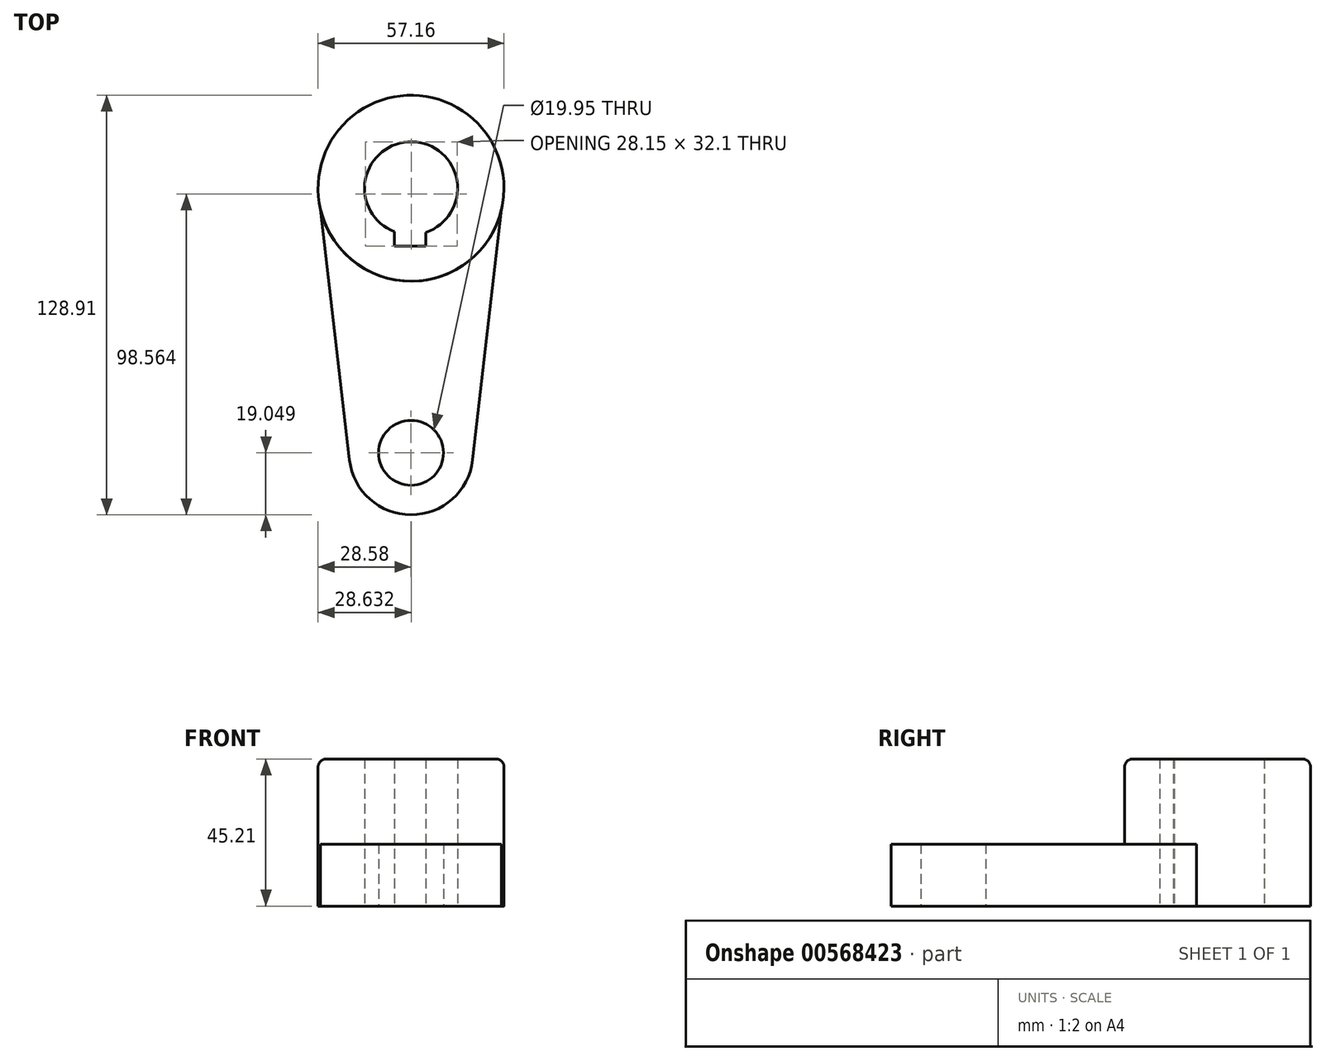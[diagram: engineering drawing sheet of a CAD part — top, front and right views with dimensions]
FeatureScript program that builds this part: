
annotation { "Feature Type Name" : "Feature", "Feature Type Description" : "" }
export const myFeature = defineFeature(function(context is Context, id is Id, definition is map)
    precondition{}
    {
        {
            var Q0;
            Q0=qCreatedBy(makeId("Top.planeOp"),FACE);
            var sketch = newSketch(context, id + "F0", { "sketchPlane" : qUnion([Q0])});
            skArc(sketch, "E0", {"start": v(28.57, 0) * mm, "mid": v(0, 28.57) * mm, "end": v(-28.57, 0) * mm});
            skArc(sketch, "E1", {"start": v(4.54, -13.55) * mm, "mid": v(0.3, 14.28) * mm, "end": v(-5.11, -13.34) * mm});
            skLineSegment(sketch, "E2", {"start": v(-5.11, -13.34) * mm, "end": v(-5.11, -17.82) * mm});
            skLineSegment(sketch, "E3", {"start": v(-5.11, -17.82) * mm, "end": v(4.54, -17.82) * mm});
            skLineSegment(sketch, "E4", {"start": v(4.54, -17.82) * mm, "end": v(4.54, -13.55) * mm});
            skArc(sketch, "E5", {"start": v(-18.92, -83.47) * mm, "mid": v(0, -100.33) * mm, "end": v(18.92, -83.47) * mm});
            skLineSegment(sketch, "E6", {"start": v(28.58, 0) * mm, "end": v(18.92, -83.47) * mm});
            skLineSegment(sketch, "E7", {"start": v(-28.58, 0) * mm, "end": v(-18.92, -83.47) * mm});
            skCircle(sketch, "E8", {"center": v(0, -81.28) * mm, "radius": 9.98 * mm});
            skSolve(sketch);
        }
        {
            var Q0;
            Q0=qCreatedBy(makeId("Top.planeOp"),FACE);
            var sketch = newSketch(context, id + "F1", { "sketchPlane" : qUnion([Q0])});
            skArc(sketch, "E9.0", {"start": v(4.54, -13.55) * mm, "mid": v(0.3, 14.28) * mm, "end": v(-5.11, -13.34) * mm});
            skLineSegment(sketch, "E10.0", {"start": v(-5.11, -17.82) * mm, "end": v(4.54, -17.82) * mm});
            skLineSegment(sketch, "E11.0", {"start": v(-5.11, -13.34) * mm, "end": v(-5.11, -17.82) * mm});
            skLineSegment(sketch, "E12.0", {"start": v(4.54, -17.82) * mm, "end": v(4.54, -13.55) * mm});
            skCircle(sketch, "E13", {"center": v(0, 0) * mm, "radius": 28.58 * mm});
            skSolve(sketch);
        }
        {
            var Q0;
            Q0 = qSketchRegion(id + "F0", true);
            extrude(context, id + "F2", {"entities" : qUnion([Q0]), "depth" : 19.05 * mm, "offsetDistance" : 25.4 * mm});
        }
        {
            var Q0;
            Q0 = qSketchRegion(id + "F1", true);
            extrude(context, id + "F3", {"entities" : qUnion([Q0]), "operationType" : NewBodyOperationType.ADD, "depth" : 45.2 * mm, "offsetDistance" : 25.4 * mm});
        }
        {
            var Q0;
            Q0=makeQuery(id+"F3.opExtrude","CAP_EDGE",EDGE,{"disambiguationData":[OSD([sQuery(id+"F1.wireOp",EDGE,"E13")])],"isStart":false});
            fillet(context, id + "F4", {"entities" : qUnion([Q0]), "radius" : 2.54 * mm, "tangentPropagation" : true, "allowEdgeOverflow" : false});
        }
    });
